# Revit family: C75-P1300 G2 40 60 WH 5000 DALI 830 PRE C2 MP_Unhosted
name_source: partatom
category: Lighting Fixtures
revit_build: Autodesk Revit 2016 (Build: 20151007_0715(x64)
units: mm (PartAtom-declared; Revit-internal decimal feet)

## family parameters
Always vertical = Yes
Cut with Voids When Loaded = No
Light Source = Yes
OmniClass Number = 23.80.70.00
OmniClass Title = Lighting
Part Type = Normal
Room Calculation Point = No
Round Connector Dimension = Use Diameter
Shared = No
Work Plane-Based = No

## types (1)
- C75-P1300 G2 40 60 WH 5000 DALI 830 PRE C2 MP_Unhosted
    # ballast on a MCB16 type B fuse = 22
    # ballast on a MCB16 type C fuse = 37
    #Ballast = 1
    Apparent Load = 36 VA
    ArticleNumber = C75234141
    Body Material and Colour = Default
    Color Filter = 16777215
    Description = C75-P1300 G2 40/60 WH 5000 DALI 830 PRE C2 MP
    Dimming Lamp Color Temperature Shift = <None>
    EANNo = 7332402341416
    Emit Shape Visible in Rendering = No
    Emit from Rectangle Length = 300 mm
    Emit from Rectangle Width = 1300 mm  [stored 4.26509 ft]
    Expired = 0
    Frequency = 50 Hz
    FrequencyMax = 60 Hz
    Glamox Category = Interior
    Glamox Family = C75-P G2
    Glamox Mounting = Pendant
    GlobalTradeItemNumber = 7332402341416
    Height = 40 mm
    IFC Classification = Light Fixture
    IPClass = 20
    IP_Code = 20
    Lamp = LED
    Length = 1306 mm  [stored 4.28478 ft]
    LightFixtureMountingType = SUSPENDED
    LightFixturePlacingType = CEILING
    LumLength = 1300 mm  [stored 4.26509 ft]
    LumWidth = 300 mm
    MFArtNo = C75234141
    MaintenanceFactor = 0
    Manufacturer = Glamox
    Maximum TA = 45
    ModelLabel = C75-P1300 G2 40/60 WH 5000 DALI 830 PRE C2 MP
    ModelReference = C75-P G2
    NominalFrequencyRange = 50 Hz
    Number of Poles = 1
    Optic = MP
    Photometric Web File = C75-P1300-G2-40-60-5000-830-MP.ies
    Power Factor = 0.98
    PowerFactor = 98.00%
    RatedVoltage = 220 V
    Specification = Interior product, in body material Aluminium, for Pendant mounting, in White  colour, IP20, light source LED, lumen out 4705lm, ballast type DALI, light source supplied type CRI>80, 3000K, 2 metre cable, optic type MP = Micro-Prismatic, with Acrylic difuser material, gives an up/down light distribution 40/60.
    Suspension Material = Default
    Suspensions Visible = No
    Termination = 5x0,75 C2
    Tilt Angle = 90.00°
    Total Load = 35 W
    TotalWattage = 35 W
    TypeOfBallast = DALI
    URL Denmark = http://glamox.com
    URL Estonia = http://glamox.com
    URL Finland = http://glamox.com
    URL Germany = http://glamox.com
    URL Ireland = http://glamox.com
    URL Norway = http://glamox.com
    URL Other = http://glamox.com
    URL Russia = http://glamox.com
    URL Sweden = http://glamox.com
    URL UK = http://glamox.com
    UpdateDate = 17.11.2020 06:31:50
    Voltage = 220 V
    VoltageMax = 240 V
    Width = 358 mm  [stored 1.17454 ft]
    Width1 = 90 mm

note: [stored X ft] marks values corroborated as IEEE doubles in the binary element streams (Revit-internal decimal feet)

## geometry (parser evidence)
native form markers: Sweep x3
no freeform markers — native parametric forms only
